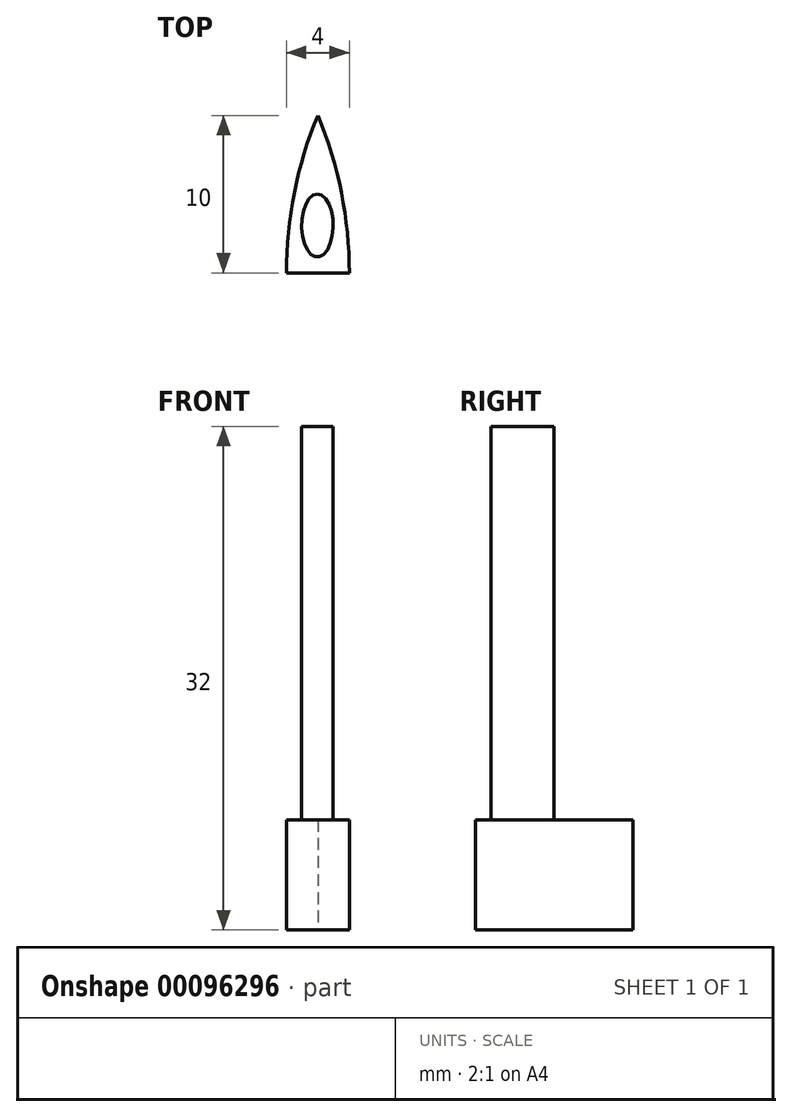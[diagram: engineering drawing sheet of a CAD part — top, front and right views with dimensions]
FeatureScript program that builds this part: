
annotation { "Feature Type Name" : "Feature", "Feature Type Description" : "" }
export const myFeature = defineFeature(function(context is Context, id is Id, definition is map)
    precondition{}
    {
        {
            var Q0;
            Q0=qCreatedBy(makeId("Top.planeOp"),FACE);
            var sketch = newSketch(context, id + "F0", { "sketchPlane" : qUnion([Q0])});
            skLineSegment(sketch, "E0.bottom", {"start": v(0, 0) * mm, "end": v(4, 0) * mm});
            skArc(sketch, "E1", {"start": v(2, 10) * mm, "mid": v(0.5, 5.1) * mm, "end": v(0, 0) * mm});
            skArc(sketch, "E2", {"start": v(4, 0) * mm, "mid": v(3.5, 5.1) * mm, "end": v(2, 10) * mm});
            skPoint(sketch, "E0.left.end.orphan", {"position": v(0, 10) * mm});
            skPoint(sketch, "E0.right.end.orphan", {"position": v(4, 10) * mm});
            skSolve(sketch);
        }
        {
            var Q0;
            Q0=makeQuery(id+"F0.imprint","IMPRINT",FACE,{"disambiguationData":[TD([[makeQuery(id+"F0.imprint","IMPRINT",EDGE,{"derivedFrom":sQuery(id+"F0.wireOp",EDGE,"E0.bottom")}),1.0]])]});
            extrude(context, id + "F1", {"entities" : qUnion([Q0]), "depth" : 7 * mm});
        }
        {
            var Q0;
            Q0=makeQuery(id+"F1.opExtrude","CAP_FACE",FACE,{"disambiguationData":[OSD([sQuery(id+"F0.wireOp",EDGE,"E0.bottom"),sQuery(id+"F0.wireOp",EDGE,"E1"),sQuery(id+"F0.wireOp",EDGE,"E2")])],"isStart":false});
            var sketch = newSketch(context, id + "F2", { "sketchPlane" : qUnion([Q0])});
            skEllipse(sketch, "E3", {"center": v(1.97, 3) * mm, "majorRadius": 2 * mm, "minorRadius": 1 * mm, "majorAxis": v(0, 1)});
            skSolve(sketch);
        }
        {
            var Q0;
            Q0=makeQuery(id+"F2.imprint","IMPRINT",FACE,{"disambiguationData":[TD([[makeQuery(id+"F2.imprint","IMPRINT",EDGE,{"derivedFrom":sQuery(id+"F2.wireOp",EDGE,"E3")}),1.0]])]});
            extrude(context, id + "F3", {"entities" : qUnion([Q0]), "operationType" : NewBodyOperationType.ADD, "depth" : 25 * mm});
        }
    });
